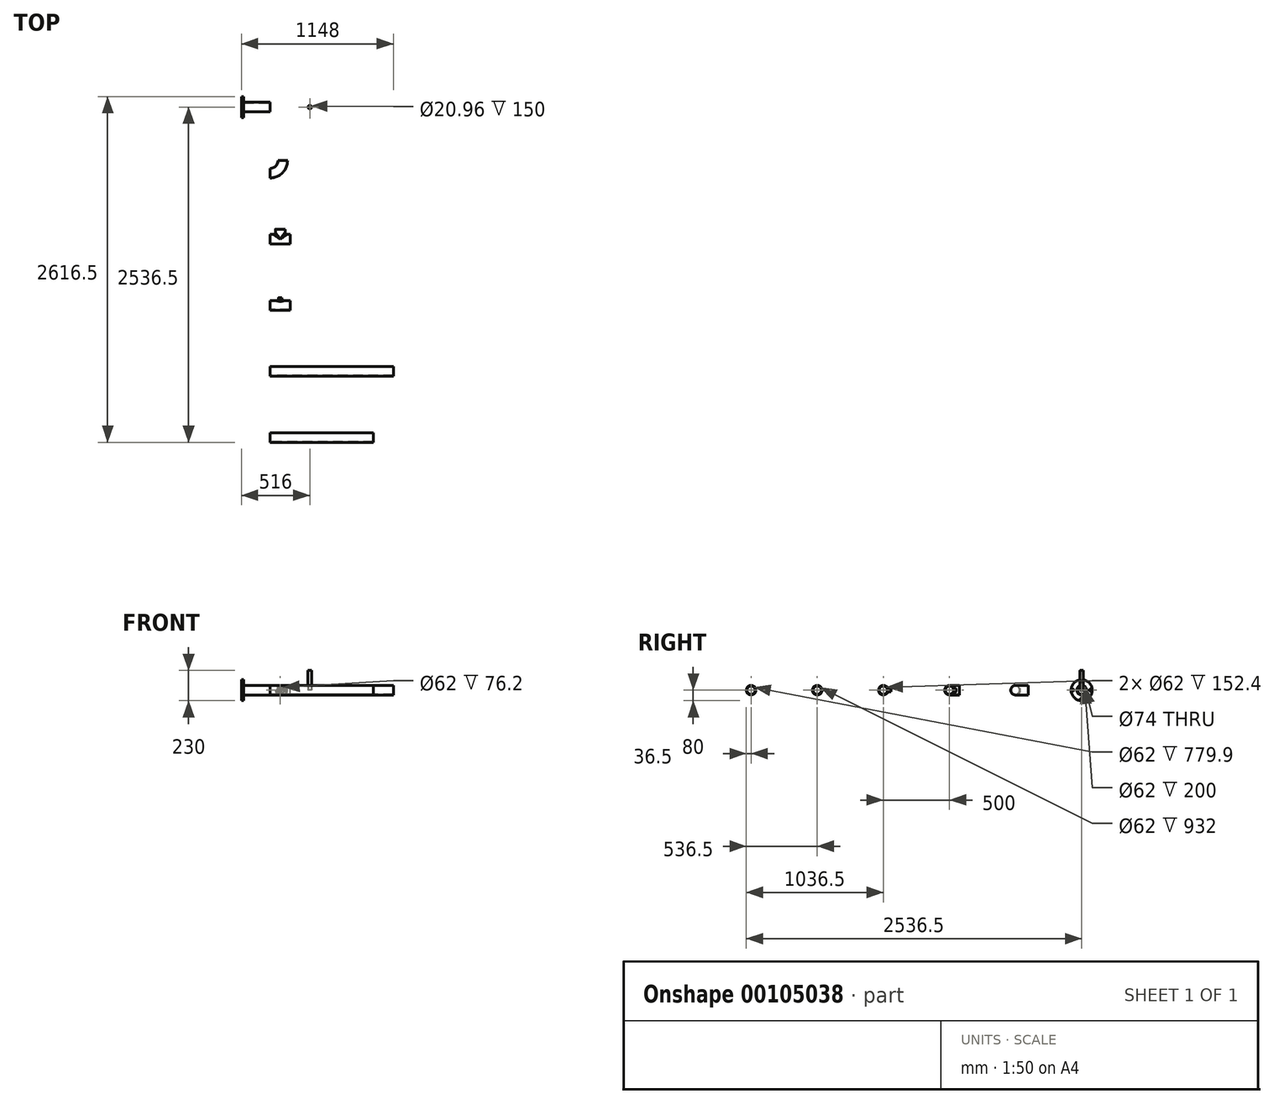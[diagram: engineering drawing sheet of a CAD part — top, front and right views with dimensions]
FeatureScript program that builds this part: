
annotation { "Feature Type Name" : "Feature", "Feature Type Description" : "" }
export const myFeature = defineFeature(function(context is Context, id is Id, definition is map)
    precondition{}
    {
        {
            assignVariable(context, id + "F0", {"name" : "B2", "anyValue" : 5.5});
        }
        {
            var Q0;
            Q0=qCreatedBy(makeId("Right.planeOp"),FACE);
            var sketch = newSketch(context, id + "F1", { "sketchPlane" : qUnion([Q0])});
            skCircle(sketch, "E0", {"center": v(0, 0) * mm, "radius": 36.5 * mm});
            skCircle(sketch, "E1", {"center": v(0, 0) * mm, "radius": 31 * mm});
            skCircle(sketch, "E2", {"center": v(-500, 0) * mm, "radius": 31 * mm});
            skCircle(sketch, "E3", {"center": v(-500, 0) * mm, "radius": 36.5 * mm});
            skCircle(sketch, "E4", {"center": v(-1000, 0) * mm, "radius": 36.5 * mm});
            skCircle(sketch, "E5", {"center": v(-1500, 0) * mm, "radius": 36.5 * mm});
            skCircle(sketch, "E6", {"center": v(-2000, 0) * mm, "radius": 36.5 * mm});
            skCircle(sketch, "E7", {"center": v(-2000, 0) * mm, "radius": 31 * mm});
            skCircle(sketch, "E8", {"center": v(-2500, 0) * mm, "radius": 36.5 * mm});
            skCircle(sketch, "E9", {"center": v(-2500, 0) * mm, "radius": 31 * mm});
            skSolve(sketch);
        }
        {
            var Q0;
            Q0=makeQuery(id+"F1.imprint","IMPRINT",FACE,{"disambiguationData":[TD([[makeQuery(id+"F1.imprint","IMPRINT",EDGE,{"derivedFrom":sQuery(id+"F1.wireOp",EDGE,"E0")}),1.0]])]});
            extrude(context, id + "F2", {"entities" : qUnion([Q0]), "oppositeDirection" : true, "depth" : 200 * mm});
        }
        {
            assignVariable(context, id + "F3", {"name" : "B6", "anyValue" : 16});
        }
        {
            assignVariable(context, id + "F4", {"name" : "B8", "anyValue" : 4});
        }
        {
            var Q0;
            Q0=makeQuery(id+"F2.opExtrude","CAP_FACE",FACE,{"disambiguationData":[OSD([sQuery(id+"F1.wireOp",EDGE,"E0"),sQuery(id+"F1.wireOp",EDGE,"E1")])],"isStart":false});
            var sketch = newSketch(context, id + "F5", { "sketchPlane" : qUnion([Q0])});
            skCircle(sketch, "E10", {"center": v(0, 0) * mm, "radius": 37 * mm});
            skCircle(sketch, "E11", {"center": v(0, 0) * mm, "radius": 80 * mm});
            skCircle(sketch, "E12", {"center": v(0, 0) * mm, "radius": 65 * mm, "construction": true});
            skCircle(sketch, "E13", {"center": v(0, 65) * mm, "radius": 7 * mm});
            skSolve(sketch);
        }
        {
            var Q0;
            Q0=makeQuery(id+"F5.imprint","IMPRINT",FACE,{"disambiguationData":[TD([[makeQuery(id+"F5.imprint","IMPRINT",EDGE,{"derivedFrom":sQuery(id+"F5.wireOp",EDGE,"E10")}),-1.0]])]});
            extrude(context, id + "F6", {"entities" : qUnion([Q0]), "depth" : (getVariable(context, 'B6')) * mm});
        }
        {
            var Q0;
            Q0=makeQuery(id+"F6.opExtrude","SWEPT_FACE",FACE,{"disambiguationData":[OSD([sQuery(id+"F5.wireOp",EDGE,"E13")])]});
            var Q1;
            Q1=makeQuery(id+"F6.opExtrude","CAP_EDGE",EDGE,{"disambiguationData":[OSD([sQuery(id+"F5.wireOp",EDGE,"E10")])],"isStart":false});
            circularPattern(context, id + "F7", {"patternType" : PatternType.FACE, "faces" : qUnion([Q0]), "axis" : qUnion([Q1]), "angle" : 360 * degree, "instanceCount" : getVariable(context, 'B8'), "equalSpace" : true});
        }
        {
            assignVariable(context, id + "F8", {"name" : "B12", "anyValue" : 150});
        }
        {
            var Q0;
            Q0=qCreatedBy(makeId("Top.planeOp"),FACE);
            var sketch = newSketch(context, id + "F9", { "sketchPlane" : qUnion([Q0])});
            skCircle(sketch, "E14", {"center": v(300, 0) * mm, "radius": 13.35 * mm});
            skCircle(sketch, "E15", {"center": v(300, 0) * mm, "radius": 10.48 * mm});
            skSolve(sketch);
        }
        {
            var Q0;
            Q0=makeQuery(id+"F9.imprint","IMPRINT",FACE,{"disambiguationData":[TD([[makeQuery(id+"F9.imprint","IMPRINT",EDGE,{"derivedFrom":sQuery(id+"F9.wireOp",EDGE,"E14")}),1.0]])]});
            extrude(context, id + "F10", {"entities" : qUnion([Q0]), "depth" : (getVariable(context, 'B12')) * mm});
        }
        {
            var Q0;
            Q0=qCreatedBy(makeId("Top.planeOp"),FACE);
            var sketch = newSketch(context, id + "F11", { "sketchPlane" : qUnion([Q0])});
            skArc(sketch, "E16", {"start": v(0, -500) * mm, "mid": v(67.18, -472.18) * mm, "end": v(95, -405) * mm});
            skLineSegment(sketch, "E17", {"start": v(0, -405) * mm, "end": v(95, -405) * mm, "construction": true});
            skLineSegment(sketch, "E18", {"start": v(0, -405) * mm, "end": v(0, -500) * mm, "construction": true});
            skLineSegment(sketch, "E19", {"start": v(0, -1000) * mm, "end": v(178.42, -1000) * mm, "construction": true});
            skLineSegment(sketch, "E20", {"start": v(0, -1500) * mm, "end": v(192.45, -1500) * mm, "construction": true});
            skSolve(sketch);
        }
        {
            var Q0;
            Q0=makeQuery(id+"F1.imprint","IMPRINT",FACE,{"disambiguationData":[TD([[makeQuery(id+"F1.imprint","IMPRINT",EDGE,{"derivedFrom":sQuery(id+"F1.wireOp",EDGE,"E2")}),-1.0]])]});
            var Q1;
            Q1=sQuery(id+"F11.wireOp",EDGE,"E16");
            sweep(context, id + "F12", {"profiles" : qUnion([Q0]), "path" : qUnion([Q1])});
        }
        {
            assignVariable(context, id + "F13", {"name" : "B14", "anyValue" : 76.2});
        }
        {
            var Q0;
            Q0=makeQuery(id+"F1.imprint","IMPRINT",FACE,{"disambiguationData":[TD([[makeQuery(id+"F1.imprint","IMPRINT",EDGE,{"derivedFrom":sQuery(id+"F1.wireOp",EDGE,"E4")}),1.0]])]});
            extrude(context, id + "F14", {"entities" : qUnion([Q0]), "depth" : (2 * getVariable(context, 'B14')) * mm});
        }
        {
            var Q0;
            Q0=sQuery(id+"F11.wireOp",EDGE,"E19");
            cPlane(context, id + "F15", {"entities" : qUnion([Q0]), "cplaneType" : CPlaneType.LINE_ANGLE, "offset" : 150 * mm, "angle" : 0 * degree, "width" : 150 * mm, "height" : 150 * mm});
        }
        {
            var Q0;
            Q0=qCreatedBy(id+"F15.planeOp",FACE);
            var sketch = newSketch(context, id + "F16", { "sketchPlane" : qUnion([Q0])});
            skCircle(sketch, "E21", {"center": v(-76.2, 0) * mm, "radius": 36.5 * mm});
            skSolve(sketch);
        }
        {
            var Q0;
            Q0=makeQuery(id+"F16.imprint","IMPRINT",FACE,{"disambiguationData":[TD([[makeQuery(id+"F16.imprint","IMPRINT",EDGE,{"derivedFrom":sQuery(id+"F16.wireOp",EDGE,"E21")}),1.0]])]});
            extrude(context, id + "F17", {"entities" : qUnion([Q0]), "operationType" : NewBodyOperationType.ADD, "depth" : (getVariable(context, 'B14')) * mm});
        }
        {
            var Q0;
            Q0=makeQuery(id+"F17.boolean.opBoolean","INTERSECT",EDGE,{"disambiguationData":[OD(0.0)],"derivedFrom":[makeQuery(id+"F14.opExtrude","SWEPT_FACE",FACE,{"disambiguationData":[OSD([sQuery(id+"F1.wireOp",EDGE,"E4")])]}),makeQuery(id+"F17.opExtrude","SWEPT_FACE",FACE,{"disambiguationData":[OSD([sQuery(id+"F16.wireOp",EDGE,"E21")])]})]});
            var Q1;
            Q1=makeQuery(id+"F17.boolean.opBoolean","INTERSECT",EDGE,{"disambiguationData":[OD(1.0)],"derivedFrom":[makeQuery(id+"F14.opExtrude","SWEPT_FACE",FACE,{"disambiguationData":[OSD([sQuery(id+"F1.wireOp",EDGE,"E4")])]}),makeQuery(id+"F17.opExtrude","SWEPT_FACE",FACE,{"disambiguationData":[OSD([sQuery(id+"F16.wireOp",EDGE,"E21")])]})]});
            fillet(context, id + "F18", {"entities" : qUnion([Q0, Q1]), "radius" : 15 * mm, "tangentPropagation" : true, "allowEdgeOverflow" : false});
        }
        {
            var Q0;
            Q0=makeQuery(id+"F17.opExtrude","CAP_FACE",FACE,{"disambiguationData":[OSD([sQuery(id+"F16.wireOp",EDGE,"E21")])],"isStart":false});
            var Q1;
            Q1=makeQuery(id+"F14.opExtrude","CAP_FACE",FACE,{"disambiguationData":[OSD([sQuery(id+"F1.wireOp",EDGE,"E4")])],"isStart":true});
            var Q2;
            Q2=makeQuery(id+"F14.opExtrude","CAP_FACE",FACE,{"disambiguationData":[OSD([sQuery(id+"F1.wireOp",EDGE,"E4")])],"isStart":false});
            shell(context, id + "F19", {"entities" : qUnion([Q0, Q1, Q2]), "thickness" : (getVariable(context, 'B2')) * mm});
        }
        {
            var Q0;
            Q0=makeQuery(id+"F1.imprint","IMPRINT",FACE,{"disambiguationData":[TD([[makeQuery(id+"F1.imprint","IMPRINT",EDGE,{"derivedFrom":sQuery(id+"F1.wireOp",EDGE,"E5")}),1.0]])]});
            extrude(context, id + "F20", {"entities" : qUnion([Q0]), "depth" : (2 * getVariable(context, 'B14')) * mm});
        }
        {
            assignVariable(context, id + "F21", {"name" : "B16", "anyValue" : 57.1});
        }
        {
            var Q0;
            Q0=sQuery(id+"F11.wireOp",EDGE,"E20");
            cPlane(context, id + "F22", {"entities" : qUnion([Q0]), "cplaneType" : CPlaneType.LINE_ANGLE, "offset" : 150 * mm, "angle" : 0 * degree, "width" : 150 * mm, "height" : 150 * mm});
        }
        {
            var Q0;
            Q0=qCreatedBy(id+"F22.planeOp",FACE);
            var sketch = newSketch(context, id + "F23", { "sketchPlane" : qUnion([Q0])});
            skCircle(sketch, "E22", {"center": v(-76.2, 0) * mm, "radius": 13.35 * mm});
            skSolve(sketch);
        }
        {
            var Q0;
            Q0=makeQuery(id+"F23.imprint","IMPRINT",FACE,{"disambiguationData":[TD([[makeQuery(id+"F23.imprint","IMPRINT",EDGE,{"derivedFrom":sQuery(id+"F23.wireOp",EDGE,"E22")}),1.0]])]});
            extrude(context, id + "F24", {"entities" : qUnion([Q0]), "operationType" : NewBodyOperationType.ADD, "depth" : (getVariable(context, 'B16')) * mm});
        }
        {
            var Q0;
            Q0=makeQuery(id+"F24.boolean.opBoolean","INTERSECT",EDGE,{"derivedFrom":[makeQuery(id+"F20.opExtrude","SWEPT_FACE",FACE,{"disambiguationData":[OSD([sQuery(id+"F1.wireOp",EDGE,"E5")])]}),makeQuery(id+"F24.opExtrude","SWEPT_FACE",FACE,{"disambiguationData":[OSD([sQuery(id+"F23.wireOp",EDGE,"E22")])]})]});
            fillet(context, id + "F25", {"entities" : qUnion([Q0]), "radius" : 15 * mm, "tangentPropagation" : true, "allowEdgeOverflow" : false});
        }
        {
            var Q0;
            Q0=makeQuery(id+"F20.opExtrude","CAP_FACE",FACE,{"disambiguationData":[OSD([sQuery(id+"F1.wireOp",EDGE,"E5")])],"isStart":false});
            var Q1;
            Q1=makeQuery(id+"F20.opExtrude","CAP_FACE",FACE,{"disambiguationData":[OSD([sQuery(id+"F1.wireOp",EDGE,"E5")])],"isStart":true});
            var Q2;
            Q2=makeQuery(id+"F24.opExtrude","CAP_FACE",FACE,{"disambiguationData":[OSD([sQuery(id+"F23.wireOp",EDGE,"E22")])],"isStart":false});
            shell(context, id + "F26", {"entities" : qUnion([Q0, Q1, Q2]), "thickness" : (getVariable(context, 'B2')) * mm});
        }
        {
            assignVariable(context, id + "F27", {"name" : "B17", "anyValue" : 932});
        }
        {
            assignVariable(context, id + "F28", {"name" : "B18", "anyValue" : 779.9});
        }
        {
            var Q0;
            Q0=makeQuery(id+"F1.imprint","IMPRINT",FACE,{"disambiguationData":[TD([[makeQuery(id+"F1.imprint","IMPRINT",EDGE,{"derivedFrom":sQuery(id+"F1.wireOp",EDGE,"E6")}),1.0]])]});
            extrude(context, id + "F29", {"entities" : qUnion([Q0]), "depth" : (getVariable(context, 'B17')) * mm});
        }
        {
            var Q0;
            Q0=makeQuery(id+"F1.imprint","IMPRINT",FACE,{"disambiguationData":[TD([[makeQuery(id+"F1.imprint","IMPRINT",EDGE,{"derivedFrom":sQuery(id+"F1.wireOp",EDGE,"E8")}),1.0]])]});
            extrude(context, id + "F30", {"entities" : qUnion([Q0]), "depth" : (getVariable(context, 'B18')) * mm});
        }
    });
